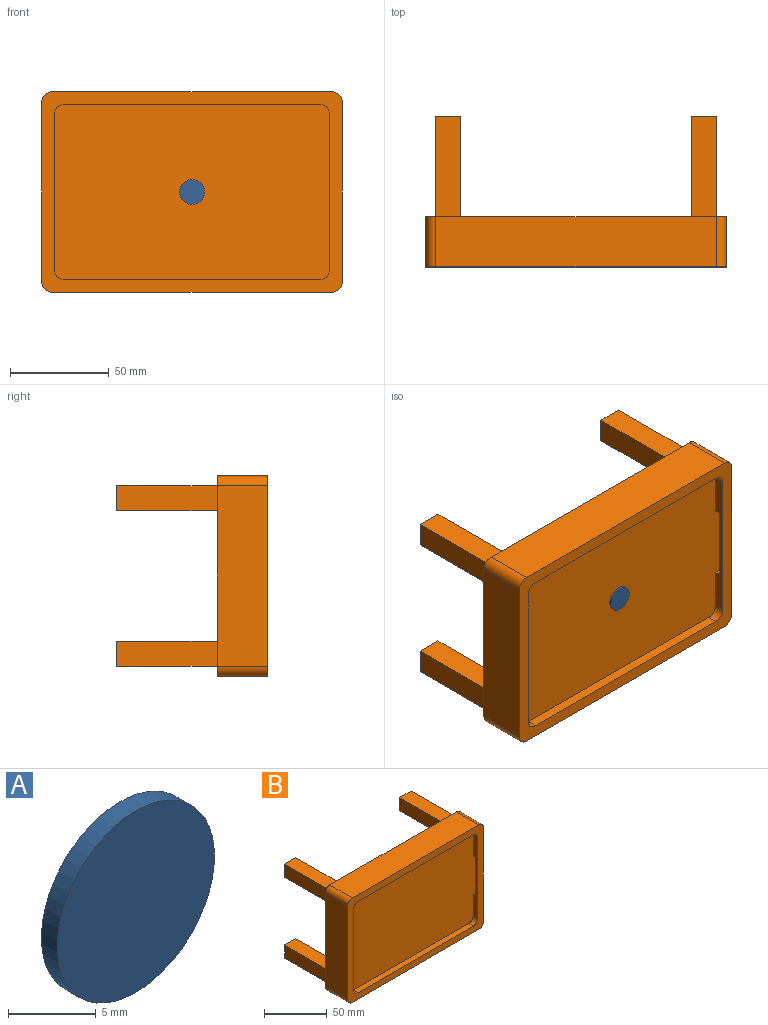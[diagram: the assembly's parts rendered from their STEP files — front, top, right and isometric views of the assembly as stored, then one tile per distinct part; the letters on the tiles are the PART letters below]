
ASSEMBLY  parts=2 mates=1
PART A: 3 faces, bbox 12.7x1.3x12.7 mm
  f0: cylinder r=6.35mm len=12.7mm, axis (0,1,0), area 50.7mm2, adj f1,f2
  f1: plane 12.7x12.7mm, normal (0,-1,0), area 126.7mm2, adj f0
  f2: plane 12.7x12.7mm, normal (0,1,0), area 126.7mm2, adj f0
PART B: 47 faces, bbox 152.4x76.2x101.6 mm
  f0: plane 78.74x5.08mm, normal (-1,0,0), area 303.2mm2, adj f6,f10,f11,f14,f23,f24,f25
  f1: plane 78.74x5.08mm, normal (1,0,0), area 303.2mm2, adj f6,f10,f12,f13,f19,f20,f21
  f2: plane 91.44x25.4mm, normal (1,0,0), area 2322.6mm2, adj f6,f7,f15,f18
  f3: plane 142.24x25.4mm, normal (0,0,1), area 3612.9mm2, adj f6,f7,f15,f16
  f4: plane 91.44x25.4mm, normal (-1,0,0), area 2322.6mm2, adj f6,f7,f16,f17
  f5: plane 142.24x25.4mm, normal (0,0,-1), area 3612.9mm2, adj f6,f7,f17,f18
  f6: plane 152.4x101.6mm, normal (0,-1,0), area 3064.5mm2, adj f0,f1,f2,f3,f4,f5,f8,f9
  f7: plane 152.4x101.6mm, normal (0,1,0), area 14816.5mm2, adj f2,f3,f4,f5,f15,f16,f17,f18
  f8: plane 129.54x5.08mm, normal (0,0,-1), area 658.1mm2, adj f6,f10,f11,f12
  f9: plane 129.54x5.08mm, normal (0,0,1), area 658.1mm2, adj f6,f10,f13,f14
  f10: plane 149.86x88.9mm, normal (0,-1,0), area 12784.3mm2, adj f0,f1,f8,f9,f11,f12,f13,f14
  f11: cylinder r=5.08mm len=5.08mm, axis (0,1,0), area 40.5mm2, adj f0,f6,f8,f10
  f12: cylinder r=5.08mm len=5.08mm, axis (0,-1,0), area 40.5mm2, adj f1,f6,f8,f10
  f13: cylinder r=5.08mm len=5.08mm, axis (0,1,0), area 40.5mm2, adj f1,f6,f9,f10
  f14: cylinder r=5.08mm len=5.08mm, axis (0,-1,0), area 40.5mm2, adj f0,f6,f9,f10
  f15: cylinder r=5.08mm len=25.4mm, axis (0,1,0), area 202.7mm2, adj f2,f3,f6,f7
  f16: cylinder r=5.08mm len=25.4mm, axis (0,-1,0), area 202.7mm2, adj f3,f4,f6,f7
  f17: cylinder r=5.08mm len=25.4mm, axis (0,1,0), area 202.7mm2, adj f4,f5,f6,f7
  f18: cylinder r=5.08mm len=25.4mm, axis (0,-1,0), area 202.7mm2, adj f2,f5,f6,f7
  f19: plane 5.08x2.54mm, normal (0,0,1), area 12.9mm2, adj f1,f10,f21,f22
  f20: plane 5.08x2.54mm, normal (0,0,-1), area 12.9mm2, adj f1,f10,f21,f22
  f21: plane 38.1x5.08mm, normal (0,1,0), area 193.5mm2, adj f1,f19,f20,f22
  f22: plane 38.1x2.54mm, normal (1,0,0), area 96.8mm2, adj f10,f19,f20,f21
  f23: plane 5.08x2.54mm, normal (0,0,1), area 12.9mm2, adj f0,f10,f24,f26
  f24: plane 38.1x5.08mm, normal (0,1,0), area 193.5mm2, adj f0,f23,f25,f26
  f25: plane 5.08x2.54mm, normal (0,0,-1), area 12.9mm2, adj f0,f10,f24,f26
  f26: plane 38.1x2.54mm, normal (-1,0,0), area 96.8mm2, adj f10,f23,f24,f25
  f27: plane 50.8x12.7mm, normal (-1,0,0), area 645.2mm2, adj f7,f28,f30,f31
  f28: plane 50.8x12.7mm, normal (0,0,1), area 645.2mm2, adj f7,f27,f29,f31
  f29: plane 50.8x12.7mm, normal (1,0,0), area 645.2mm2, adj f7,f28,f30,f31
  f30: plane 50.8x12.7mm, normal (0,0,-1), area 645.2mm2, adj f7,f27,f29,f31
  f31: plane 12.7x12.7mm, normal (0,1,0), area 161.3mm2, adj f27,f28,f29,f30
  f32: plane 50.8x12.7mm, normal (0,0,-1), area 645.2mm2, adj f7,f33,f35,f36
  f33: plane 50.8x12.7mm, normal (-1,0,0), area 645.2mm2, adj f7,f32,f34,f36
  f34: plane 50.8x12.7mm, normal (0,0,1), area 645.2mm2, adj f7,f33,f35,f36
  f35: plane 50.8x12.7mm, normal (1,0,0), area 645.2mm2, adj f7,f32,f34,f36
  f36: plane 12.7x12.7mm, normal (0,1,0), area 161.3mm2, adj f32,f33,f34,f35
  f37: plane 50.8x12.7mm, normal (0,0,1), area 645.2mm2, adj f7,f38,f40,f41
  f38: plane 50.8x12.7mm, normal (1,0,0), area 645.2mm2, adj f7,f37,f39,f41
  f39: plane 50.8x12.7mm, normal (0,0,-1), area 645.2mm2, adj f7,f38,f40,f41
  f40: plane 50.8x12.7mm, normal (-1,0,0), area 645.2mm2, adj f7,f37,f39,f41
  f41: plane 12.7x12.7mm, normal (0,1,0), area 161.3mm2, adj f37,f38,f39,f40
  f42: plane 50.8x12.7mm, normal (1,0,0), area 645.2mm2, adj f7,f43,f45,f46
  f43: plane 50.8x12.7mm, normal (0,0,-1), area 645.2mm2, adj f7,f42,f44,f46
  f44: plane 50.8x12.7mm, normal (-1,0,0), area 645.2mm2, adj f7,f43,f45,f46
  f45: plane 50.8x12.7mm, normal (0,0,1), area 645.2mm2, adj f7,f42,f44,f46
  f46: plane 12.7x12.7mm, normal (0,1,0), area 161.3mm2, adj f42,f43,f44,f45
PLACE A t=(3.37,-19.61,17.19)mm
PLACE B t=(3.37,-11.99,17.19)mm
MATE planar A.f0 <-> B.f10  axis (0,1,0) through (3.37,-19.61,17.19)mm
